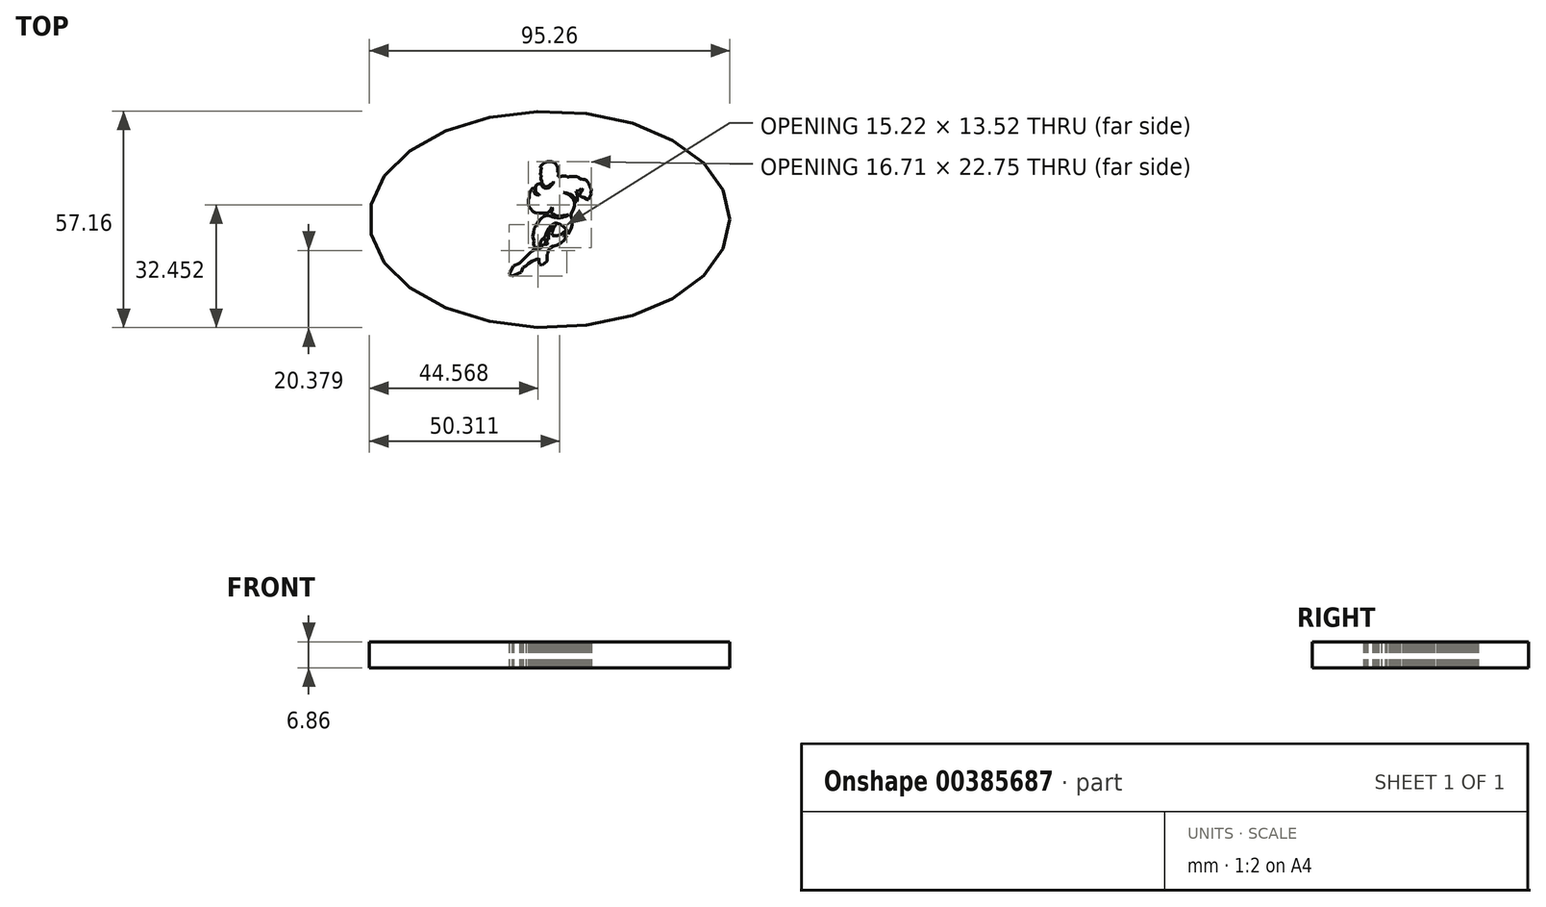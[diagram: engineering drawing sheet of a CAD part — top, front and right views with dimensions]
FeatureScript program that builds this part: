
annotation { "Feature Type Name" : "Feature", "Feature Type Description" : "" }
export const myFeature = defineFeature(function(context is Context, id is Id, definition is map)
    precondition{}
    {
        {
            var Q0;
            Q0=qCreatedBy(makeId("Top.planeOp"),FACE);
            var sketch = newSketch(context, id + "F0", { "sketchPlane" : qUnion([Q0])});
            skEllipse(sketch, "E0", {"center": v(0, 0) * mm, "majorRadius": 47.63 * mm, "minorRadius": 28.58 * mm, "majorAxis": v(1, 0)});
            skLineSegment(sketch, "E1", {"start": v(-10.67, -14.48) * mm, "end": v(-9.93, -14.96) * mm});
            skLineSegment(sketch, "E2", {"start": v(-9.93, -14.96) * mm, "end": v(-7.5, -13.97) * mm});
            skLineSegment(sketch, "E3", {"start": v(-7.5, -13.97) * mm, "end": v(-6.98, -12.63) * mm});
            skLineSegment(sketch, "E4", {"start": v(-6.98, -12.63) * mm, "end": v(-6.3, -12.34) * mm});
            skLineSegment(sketch, "E5", {"start": v(-6.3, -12.34) * mm, "end": v(-5.68, -11.68) * mm});
            skLineSegment(sketch, "E6", {"start": v(-5.68, -11.68) * mm, "end": v(-4.62, -11.01) * mm});
            skLineSegment(sketch, "E7", {"start": v(-4.62, -11.01) * mm, "end": v(-2.83, -10.28) * mm});
            skLineSegment(sketch, "E8", {"start": v(-2.83, -10.28) * mm, "end": v(-2.83, -11.24) * mm});
            skLineSegment(sketch, "E9", {"start": v(-2.83, -11.24) * mm, "end": v(-2.55, -11.87) * mm});
            skLineSegment(sketch, "E10", {"start": v(-2.55, -11.87) * mm, "end": v(-1.92, -12.02) * mm});
            skLineSegment(sketch, "E11", {"start": v(-1.92, -12.02) * mm, "end": v(-0.71, -11.01) * mm});
            skLineSegment(sketch, "E12", {"start": v(-0.71, -11.01) * mm, "end": v(-0.71, -9.22) * mm});
            skLineSegment(sketch, "E13", {"start": v(-0.71, -9.22) * mm, "end": v(-0.37, -8.9) * mm});
            skLineSegment(sketch, "E14", {"start": v(-0.37, -8.9) * mm, "end": v(-0.37, -8.25) * mm});
            skLineSegment(sketch, "E15", {"start": v(-0.37, -8.25) * mm, "end": v(0.2, -7.41) * mm});
            skLineSegment(sketch, "E16", {"start": v(0.2, -7.41) * mm, "end": v(0.84, -7.05) * mm});
            skLineSegment(sketch, "E17", {"start": v(0.84, -7.05) * mm, "end": v(1.82, -6.79) * mm});
            skLineSegment(sketch, "E18", {"start": v(1.82, -6.79) * mm, "end": v(2.96, -6.26) * mm});
            skLineSegment(sketch, "E19", {"start": v(2.96, -6.26) * mm, "end": v(3.94, -5.48) * mm});
            skLineSegment(sketch, "E20", {"start": v(3.94, -5.48) * mm, "end": v(4.55, -4.27) * mm});
            skLineSegment(sketch, "E21", {"start": v(4.55, -4.27) * mm, "end": v(4.1, -4.46) * mm});
            skLineSegment(sketch, "E22", {"start": v(4.1, -4.46) * mm, "end": v(3.73, -4.6) * mm});
            skLineSegment(sketch, "E23", {"start": v(3.73, -4.6) * mm, "end": v(3.61, -4.27) * mm});
            skLineSegment(sketch, "E24", {"start": v(3.61, -4.27) * mm, "end": v(3.85, -3.8) * mm});
            skLineSegment(sketch, "E25", {"start": v(3.85, -3.8) * mm, "end": v(4.29, -3.23) * mm});
            skLineSegment(sketch, "E26", {"start": v(4.29, -3.23) * mm, "end": v(4.29, -2.92) * mm});
            skLineSegment(sketch, "E27", {"start": v(4.29, -2.92) * mm, "end": v(3.55, -3.48) * mm});
            skLineSegment(sketch, "E28", {"start": v(3.55, -3.48) * mm, "end": v(2.96, -3.88) * mm});
            skLineSegment(sketch, "E29", {"start": v(2.96, -3.88) * mm, "end": v(1.96, -4.27) * mm});
            skLineSegment(sketch, "E30", {"start": v(1.96, -4.27) * mm, "end": v(1.6, -4.27) * mm});
            skLineSegment(sketch, "E31", {"start": v(1.6, -4.27) * mm, "end": v(0.96, -4.27) * mm});
            skLineSegment(sketch, "E32", {"start": v(0.96, -4.27) * mm, "end": v(0.72, -4.15) * mm});
            skLineSegment(sketch, "E33", {"start": v(0.72, -4.15) * mm, "end": v(0.57, -3.48) * mm});
            skLineSegment(sketch, "E34", {"start": v(0.57, -3.48) * mm, "end": v(0.8, -2.73) * mm});
            skLineSegment(sketch, "E35", {"start": v(0.8, -2.73) * mm, "end": v(1.16, -2.04) * mm});
            skLineSegment(sketch, "E36", {"start": v(1.16, -2.04) * mm, "end": v(1.52, -1.7) * mm});
            skLineSegment(sketch, "E37", {"start": v(1.52, -1.7) * mm, "end": v(1.52, -1.44) * mm});
            skLineSegment(sketch, "E38", {"start": v(1.52, -1.44) * mm, "end": v(0.57, -2.4) * mm});
            skLineSegment(sketch, "E39", {"start": v(0.57, -2.4) * mm, "end": v(0, -3.06) * mm});
            skLineSegment(sketch, "E40", {"start": v(0, -3.06) * mm, "end": v(-0.25, -3.56) * mm});
            skLineSegment(sketch, "E41", {"start": v(-0.25, -3.56) * mm, "end": v(-0.25, -4.27) * mm});
            skLineSegment(sketch, "E42", {"start": v(-0.25, -4.27) * mm, "end": v(-0.25, -4.93) * mm});
            skLineSegment(sketch, "E43", {"start": v(-0.25, -4.93) * mm, "end": v(-0.25, -5.3) * mm});
            skLineSegment(sketch, "E44", {"start": v(-0.25, -5.3) * mm, "end": v(-0.71, -5.3) * mm});
            skLineSegment(sketch, "E45", {"start": v(-0.71, -5.3) * mm, "end": v(-1.08, -5.48) * mm});
            skLineSegment(sketch, "E46", {"start": v(-1.08, -5.48) * mm, "end": v(-1.38, -5.78) * mm});
            skLineSegment(sketch, "E47", {"start": v(-1.38, -5.78) * mm, "end": v(-1, -5.97) * mm});
            skLineSegment(sketch, "E48", {"start": v(-1, -5.97) * mm, "end": v(-0.71, -6.12) * mm});
            skLineSegment(sketch, "E49", {"start": v(-0.71, -6.12) * mm, "end": v(-0.57, -6.26) * mm});
            skLineSegment(sketch, "E50", {"start": v(-0.57, -6.26) * mm, "end": v(-0.57, -6.42) * mm});
            skLineSegment(sketch, "E51", {"start": v(-0.57, -6.42) * mm, "end": v(-0.67, -6.62) * mm});
            skLineSegment(sketch, "E52", {"start": v(-0.67, -6.62) * mm, "end": v(-1.6, -6.62) * mm});
            skLineSegment(sketch, "E53", {"start": v(-1.6, -6.62) * mm, "end": v(-1.92, -6.79) * mm});
            skLineSegment(sketch, "E54", {"start": v(-1.92, -6.79) * mm, "end": v(-2.1, -7.15) * mm});
            skLineSegment(sketch, "E55", {"start": v(-2.1, -7.15) * mm, "end": v(-2.1, -7.3) * mm});
            skLineSegment(sketch, "E56", {"start": v(-2.1, -7.3) * mm, "end": v(-2.83, -7.76) * mm});
            skLineSegment(sketch, "E57", {"start": v(-2.83, -7.76) * mm, "end": v(-3.27, -7.92) * mm});
            skLineSegment(sketch, "E58", {"start": v(-3.27, -7.92) * mm, "end": v(-3.6, -7.92) * mm});
            skLineSegment(sketch, "E59", {"start": v(-3.6, -7.92) * mm, "end": v(-3.79, -7.82) * mm});
            skLineSegment(sketch, "E60", {"start": v(-3.79, -7.82) * mm, "end": v(-4.48, -8.25) * mm});
            skLineSegment(sketch, "E61", {"start": v(-4.48, -8.25) * mm, "end": v(-5.33, -9.01) * mm});
            skLineSegment(sketch, "E62", {"start": v(-5.33, -9.01) * mm, "end": v(-7.95, -11.55) * mm});
            skLineSegment(sketch, "E63", {"start": v(-7.95, -11.55) * mm, "end": v(-9.63, -12.34) * mm});
            skLineSegment(sketch, "E64", {"start": v(-9.63, -12.34) * mm, "end": v(-10.67, -14.48) * mm});
            skLineSegment(sketch, "E65", {"start": v(2.2, 11.29) * mm, "end": v(2.34, 12.27) * mm});
            skLineSegment(sketch, "E66", {"start": v(2.34, 12.27) * mm, "end": v(2.1, 12.51) * mm});
            skLineSegment(sketch, "E67", {"start": v(2.1, 12.51) * mm, "end": v(2.1, 13.38) * mm});
            skLineSegment(sketch, "E68", {"start": v(2.1, 13.38) * mm, "end": v(2.1, 13.78) * mm});
            skLineSegment(sketch, "E69", {"start": v(2.1, 13.78) * mm, "end": v(1.86, 14.18) * mm});
            skLineSegment(sketch, "E70", {"start": v(1.86, 14.18) * mm, "end": v(1.64, 14.56) * mm});
            skLineSegment(sketch, "E71", {"start": v(1.64, 14.56) * mm, "end": v(1.17, 15.02) * mm});
            skLineSegment(sketch, "E72", {"start": v(1.17, 15.02) * mm, "end": v(0.53, 15.25) * mm});
            skLineSegment(sketch, "E73", {"start": v(0.53, 15.25) * mm, "end": v(-0.53, 15.25) * mm});
            skLineSegment(sketch, "E74", {"start": v(-0.53, 15.25) * mm, "end": v(-1.26, 14.98) * mm});
            skLineSegment(sketch, "E75", {"start": v(-1.26, 14.98) * mm, "end": v(-1.98, 14.52) * mm});
            skLineSegment(sketch, "E76", {"start": v(-1.98, 14.52) * mm, "end": v(-2.16, 14.18) * mm});
            skLineSegment(sketch, "E77", {"start": v(-2.16, 14.18) * mm, "end": v(-2.5, 14.04) * mm});
            skLineSegment(sketch, "E78", {"start": v(-2.5, 14.04) * mm, "end": v(-2.5, 13.78) * mm});
            skLineSegment(sketch, "E79", {"start": v(-2.5, 13.78) * mm, "end": v(-2.34, 13.72) * mm});
            skLineSegment(sketch, "E80", {"start": v(-2.34, 13.72) * mm, "end": v(-2.23, 13.72) * mm});
            skLineSegment(sketch, "E81", {"start": v(-2.23, 13.72) * mm, "end": v(-2.23, 13.34) * mm});
            skLineSegment(sketch, "E82", {"start": v(-2.23, 13.34) * mm, "end": v(-2.35, 13.14) * mm});
            skLineSegment(sketch, "E83", {"start": v(-2.35, 13.14) * mm, "end": v(-2.35, 12.76) * mm});
            skLineSegment(sketch, "E84", {"start": v(-2.35, 12.76) * mm, "end": v(-2.28, 12.66) * mm});
            skLineSegment(sketch, "E85", {"start": v(-2.28, 12.66) * mm, "end": v(-2.28, 12.42) * mm});
            skLineSegment(sketch, "E86", {"start": v(-2.28, 12.42) * mm, "end": v(-2.28, 12.24) * mm});
            skLineSegment(sketch, "E87", {"start": v(-2.28, 12.24) * mm, "end": v(-2.46, 12.17) * mm});
            skLineSegment(sketch, "E88", {"start": v(-2.46, 12.17) * mm, "end": v(-2.46, 11.86) * mm});
            skLineSegment(sketch, "E89", {"start": v(-2.46, 11.86) * mm, "end": v(-2.23, 11.6) * mm});
            skLineSegment(sketch, "E90", {"start": v(-2.23, 11.6) * mm, "end": v(-2.23, 11.3) * mm});
            skLineSegment(sketch, "E91", {"start": v(-2.23, 11.3) * mm, "end": v(-2.32, 11.19) * mm});
            skLineSegment(sketch, "E92", {"start": v(-2.32, 11.19) * mm, "end": v(-2.32, 10.68) * mm});
            skLineSegment(sketch, "E93", {"start": v(-2.32, 10.68) * mm, "end": v(-2.03, 10.04) * mm});
            skLineSegment(sketch, "E94", {"start": v(-2.03, 10.04) * mm, "end": v(-2.03, 9.67) * mm});
            skLineSegment(sketch, "E95", {"start": v(-2.03, 9.67) * mm, "end": v(-1.83, 9.43) * mm});
            skLineSegment(sketch, "E96", {"start": v(-1.83, 9.43) * mm, "end": v(-1.74, 9.17) * mm});
            skLineSegment(sketch, "E97", {"start": v(-1.74, 9.17) * mm, "end": v(-1.74, 8.9) * mm});
            skLineSegment(sketch, "E98", {"start": v(-1.74, 8.9) * mm, "end": v(-1.54, 8.72) * mm});
            skLineSegment(sketch, "E99", {"start": v(-1.54, 8.72) * mm, "end": v(-1.24, 8.63) * mm});
            skLineSegment(sketch, "E100", {"start": v(-1.24, 8.63) * mm, "end": v(-0.77, 8.7) * mm});
            skLineSegment(sketch, "E101", {"start": v(-0.77, 8.7) * mm, "end": v(-0.45, 8.81) * mm});
            skLineSegment(sketch, "E102", {"start": v(-0.45, 8.81) * mm, "end": v(0.1, 9.12) * mm});
            skLineSegment(sketch, "E103", {"start": v(0.1, 9.12) * mm, "end": v(0.57, 9.41) * mm});
            skLineSegment(sketch, "E104", {"start": v(0.57, 9.41) * mm, "end": v(0.91, 9.86) * mm});
            skLineSegment(sketch, "E105", {"start": v(0.91, 9.86) * mm, "end": v(1, 9.99) * mm});
            skLineSegment(sketch, "E106", {"start": v(1, 9.99) * mm, "end": v(1, 9.69) * mm});
            skLineSegment(sketch, "E107", {"start": v(1, 9.69) * mm, "end": v(0.85, 9.46) * mm});
            skLineSegment(sketch, "E108", {"start": v(0.85, 9.46) * mm, "end": v(0.6, 9.1) * mm});
            skLineSegment(sketch, "E109", {"start": v(0.6, 9.1) * mm, "end": v(0.08, 8.65) * mm});
            skLineSegment(sketch, "E110", {"start": v(0.08, 8.65) * mm, "end": v(-0.5, 8.3) * mm});
            skLineSegment(sketch, "E111", {"start": v(-0.5, 8.3) * mm, "end": v(-0.98, 8.3) * mm});
            skLineSegment(sketch, "E112", {"start": v(-0.98, 8.3) * mm, "end": v(-1.4, 8.3) * mm});
            skLineSegment(sketch, "E113", {"start": v(-1.4, 8.3) * mm, "end": v(-1.76, 8.55) * mm});
            skLineSegment(sketch, "E114", {"start": v(-1.76, 8.55) * mm, "end": v(-2.09, 9.08) * mm});
            skLineSegment(sketch, "E115", {"start": v(-2.09, 9.08) * mm, "end": v(-2.09, 9.48) * mm});
            skLineSegment(sketch, "E116", {"start": v(-2.09, 9.48) * mm, "end": v(-2.66, 9.48) * mm});
            skLineSegment(sketch, "E117", {"start": v(-2.66, 9.48) * mm, "end": v(-3.18, 9.3) * mm});
            skLineSegment(sketch, "E118", {"start": v(-3.18, 9.3) * mm, "end": v(-3.57, 9.06) * mm});
            skLineSegment(sketch, "E119", {"start": v(-3.57, 9.06) * mm, "end": v(-3.74, 8.45) * mm});
            skLineSegment(sketch, "E120", {"start": v(-3.74, 8.45) * mm, "end": v(-3.74, 7.87) * mm});
            skLineSegment(sketch, "E121", {"start": v(-3.74, 7.87) * mm, "end": v(-3.58, 7.18) * mm});
            skLineSegment(sketch, "E122", {"start": v(-3.58, 7.18) * mm, "end": v(-3.13, 6.77) * mm});
            skLineSegment(sketch, "E123", {"start": v(-3.13, 6.77) * mm, "end": v(-2.73, 6.53) * mm});
            skLineSegment(sketch, "E124", {"start": v(-2.73, 6.53) * mm, "end": v(-2.73, 6.38) * mm});
            skLineSegment(sketch, "E125", {"start": v(-2.73, 6.38) * mm, "end": v(-3.37, 6.53) * mm});
            skLineSegment(sketch, "E126", {"start": v(-3.37, 6.53) * mm, "end": v(-3.82, 6.8) * mm});
            skLineSegment(sketch, "E127", {"start": v(-3.82, 6.8) * mm, "end": v(-4.17, 7.18) * mm});
            skLineSegment(sketch, "E128", {"start": v(-4.17, 7.18) * mm, "end": v(-4.3, 7.6) * mm});
            skLineSegment(sketch, "E129", {"start": v(-4.3, 7.6) * mm, "end": v(-4.17, 8.28) * mm});
            skLineSegment(sketch, "E130", {"start": v(-4.17, 8.28) * mm, "end": v(-4.56, 8.1) * mm});
            skLineSegment(sketch, "E131", {"start": v(-4.56, 8.1) * mm, "end": v(-5, 7.7) * mm});
            skLineSegment(sketch, "E132", {"start": v(-5, 7.7) * mm, "end": v(-5.27, 7.18) * mm});
            skLineSegment(sketch, "E133", {"start": v(-5.27, 7.18) * mm, "end": v(-5.38, 6.72) * mm});
            skLineSegment(sketch, "E134", {"start": v(-5.38, 6.72) * mm, "end": v(-5.38, 6.33) * mm});
            skLineSegment(sketch, "E135", {"start": v(-5.38, 6.33) * mm, "end": v(-5.38, 5.89) * mm});
            skLineSegment(sketch, "E136", {"start": v(-5.38, 5.89) * mm, "end": v(-5.54, 5.53) * mm});
            skLineSegment(sketch, "E137", {"start": v(-5.54, 5.53) * mm, "end": v(-5.68, 5.21) * mm});
            skLineSegment(sketch, "E138", {"start": v(-5.68, 5.21) * mm, "end": v(-5.68, 4.35) * mm});
            skLineSegment(sketch, "E139", {"start": v(-5.68, 4.35) * mm, "end": v(-5.56, 3.61) * mm});
            skLineSegment(sketch, "E140", {"start": v(-5.56, 3.61) * mm, "end": v(-5.28, 3.05) * mm});
            skLineSegment(sketch, "E141", {"start": v(-5.28, 3.05) * mm, "end": v(-4.92, 2.66) * mm});
            skLineSegment(sketch, "E142", {"start": v(-4.92, 2.66) * mm, "end": v(-4.58, 2.28) * mm});
            skLineSegment(sketch, "E143", {"start": v(-4.58, 2.28) * mm, "end": v(-4.4, 2.08) * mm});
            skLineSegment(sketch, "E144", {"start": v(-4.4, 2.08) * mm, "end": v(-3.89, 1.76) * mm});
            skLineSegment(sketch, "E145", {"start": v(-3.89, 1.76) * mm, "end": v(-3.25, 1.62) * mm});
            skLineSegment(sketch, "E146", {"start": v(-3.25, 1.62) * mm, "end": v(-0.96, 1.62) * mm});
            skLineSegment(sketch, "E147", {"start": v(-0.96, 1.62) * mm, "end": v(-0.43, 1.83) * mm});
            skLineSegment(sketch, "E148", {"start": v(-0.43, 1.83) * mm, "end": v(0, 2.22) * mm});
            skLineSegment(sketch, "E149", {"start": v(0, 2.22) * mm, "end": v(0.3, 2.5) * mm});
            skLineSegment(sketch, "E150", {"start": v(0.3, 2.5) * mm, "end": v(0.48, 3.03) * mm});
            skLineSegment(sketch, "E151", {"start": v(0.48, 3.03) * mm, "end": v(0.6, 3.14) * mm});
            skLineSegment(sketch, "E152", {"start": v(0.6, 3.14) * mm, "end": v(0.7, 2.8) * mm});
            skLineSegment(sketch, "E153", {"start": v(0.7, 2.8) * mm, "end": v(0.7, 2.36) * mm});
            skLineSegment(sketch, "E154", {"start": v(0.7, 2.36) * mm, "end": v(0.43, 1.87) * mm});
            skLineSegment(sketch, "E155", {"start": v(0.43, 1.87) * mm, "end": v(0.43, 1.66) * mm});
            skLineSegment(sketch, "E156", {"start": v(0.43, 1.66) * mm, "end": v(0.8, 1.37) * mm});
            skLineSegment(sketch, "E157", {"start": v(0.8, 1.37) * mm, "end": v(1.44, 1.09) * mm});
            skLineSegment(sketch, "E158", {"start": v(1.44, 1.09) * mm, "end": v(2.09, 0.94) * mm});
            skLineSegment(sketch, "E159", {"start": v(2.09, 0.94) * mm, "end": v(3, 0.94) * mm});
            skLineSegment(sketch, "E160", {"start": v(3, 0.94) * mm, "end": v(3.6, 1) * mm});
            skLineSegment(sketch, "E161", {"start": v(3.6, 1) * mm, "end": v(4.08, 1.05) * mm});
            skLineSegment(sketch, "E162", {"start": v(4.08, 1.05) * mm, "end": v(5, 1.3) * mm});
            skLineSegment(sketch, "E163", {"start": v(5, 1.3) * mm, "end": v(4.8, 1.04) * mm});
            skLineSegment(sketch, "E164", {"start": v(4.8, 1.04) * mm, "end": v(4.33, 0.84) * mm});
            skLineSegment(sketch, "E165", {"start": v(4.33, 0.84) * mm, "end": v(4.04, 0.72) * mm});
            skLineSegment(sketch, "E166", {"start": v(4.04, 0.72) * mm, "end": v(3.38, 0.52) * mm});
            skLineSegment(sketch, "E167", {"start": v(3.38, 0.52) * mm, "end": v(2.8, 0.4) * mm});
            skLineSegment(sketch, "E168", {"start": v(2.8, 0.4) * mm, "end": v(1.97, 0.4) * mm});
            skLineSegment(sketch, "E169", {"start": v(1.97, 0.4) * mm, "end": v(1.24, 0.52) * mm});
            skLineSegment(sketch, "E170", {"start": v(1.24, 0.52) * mm, "end": v(0.72, 0.68) * mm});
            skLineSegment(sketch, "E171", {"start": v(0.72, 0.68) * mm, "end": v(0.1, 0.94) * mm});
            skLineSegment(sketch, "E172", {"start": v(0.1, 0.94) * mm, "end": v(-0.43, 1.09) * mm});
            skLineSegment(sketch, "E173", {"start": v(-0.43, 1.09) * mm, "end": v(-0.68, 1.09) * mm});
            skLineSegment(sketch, "E174", {"start": v(-0.68, 1.09) * mm, "end": v(-1.55, 0.77) * mm});
            skLineSegment(sketch, "E175", {"start": v(-1.55, 0.77) * mm, "end": v(-2.26, 0.22) * mm});
            skLineSegment(sketch, "E176", {"start": v(-2.26, 0.22) * mm, "end": v(-3, -0.57) * mm});
            skLineSegment(sketch, "E177", {"start": v(-3, -0.57) * mm, "end": v(-3.64, -1.67) * mm});
            skLineSegment(sketch, "E178", {"start": v(-3.64, -1.67) * mm, "end": v(-4.05, -2.42) * mm});
            skLineSegment(sketch, "E179", {"start": v(-4.05, -2.42) * mm, "end": v(-4.27, -3.45) * mm});
            skLineSegment(sketch, "E180", {"start": v(-4.27, -3.45) * mm, "end": v(-4.44, -4.6) * mm});
            skLineSegment(sketch, "E181", {"start": v(-4.44, -4.6) * mm, "end": v(-4.05, -5.72) * mm});
            skLineSegment(sketch, "E182", {"start": v(-4.05, -5.72) * mm, "end": v(-4.3, -6.17) * mm});
            skLineSegment(sketch, "E183", {"start": v(-4.3, -6.17) * mm, "end": v(-4.27, -6.63) * mm});
            skLineSegment(sketch, "E184", {"start": v(-4.27, -6.63) * mm, "end": v(-4.08, -7.03) * mm});
            skLineSegment(sketch, "E185", {"start": v(-4.08, -7.03) * mm, "end": v(-3.83, -7.36) * mm});
            skLineSegment(sketch, "E186", {"start": v(-3.83, -7.36) * mm, "end": v(-3.57, -7.5) * mm});
            skLineSegment(sketch, "E187", {"start": v(-3.57, -7.5) * mm, "end": v(-2.84, -7.17) * mm});
            skLineSegment(sketch, "E188", {"start": v(-2.84, -7.17) * mm, "end": v(-2.4, -6.8) * mm});
            skLineSegment(sketch, "E189", {"start": v(-2.4, -6.8) * mm, "end": v(-2.42, -6.35) * mm});
            skLineSegment(sketch, "E190", {"start": v(-2.42, -6.35) * mm, "end": v(-2.31, -5.87) * mm});
            skLineSegment(sketch, "E191", {"start": v(-2.31, -5.87) * mm, "end": v(-2.02, -5.32) * mm});
            skLineSegment(sketch, "E192", {"start": v(-2.02, -5.32) * mm, "end": v(-1.5, -4.78) * mm});
            skLineSegment(sketch, "E193", {"start": v(-1.5, -4.78) * mm, "end": v(-1.16, -4.52) * mm});
            skLineSegment(sketch, "E194", {"start": v(-1.16, -4.52) * mm, "end": v(-0.99, -3.79) * mm});
            skLineSegment(sketch, "E195", {"start": v(-0.99, -3.79) * mm, "end": v(-0.7, -3.18) * mm});
            skLineSegment(sketch, "E196", {"start": v(-0.7, -3.18) * mm, "end": v(-0.19, -2.25) * mm});
            skLineSegment(sketch, "E197", {"start": v(-0.19, -2.25) * mm, "end": v(0.34, -1.62) * mm});
            skLineSegment(sketch, "E198", {"start": v(0.34, -1.62) * mm, "end": v(1.18, -1.03) * mm});
            skLineSegment(sketch, "E199", {"start": v(1.18, -1.03) * mm, "end": v(1.83, -1.03) * mm});
            skLineSegment(sketch, "E200", {"start": v(1.83, -1.03) * mm, "end": v(2.65, -1.28) * mm});
            skLineSegment(sketch, "E201", {"start": v(2.65, -1.28) * mm, "end": v(3.52, -1.75) * mm});
            skLineSegment(sketch, "E202", {"start": v(3.52, -1.75) * mm, "end": v(4.19, -2.42) * mm});
            skLineSegment(sketch, "E203", {"start": v(4.19, -2.42) * mm, "end": v(4.67, -2.94) * mm});
            skLineSegment(sketch, "E204", {"start": v(4.67, -2.94) * mm, "end": v(4.93, -3.91) * mm});
            skLineSegment(sketch, "E205", {"start": v(4.93, -3.91) * mm, "end": v(5.19, -3.43) * mm});
            skPoint(sketch, "E205.endSnap0", {"position": v(4.8, -3.43) * mm});
            skLineSegment(sketch, "E206", {"start": v(5.19, -3.43) * mm, "end": v(5.74, -2.42) * mm});
            skLineSegment(sketch, "E207", {"start": v(5.74, -2.42) * mm, "end": v(5.98, -1.48) * mm});
            skLineSegment(sketch, "E208", {"start": v(5.98, -1.48) * mm, "end": v(5.98, -0.83) * mm});
            skLineSegment(sketch, "E209", {"start": v(5.98, -0.83) * mm, "end": v(5.98, 0) * mm});
            skLineSegment(sketch, "E210", {"start": v(5.98, 0) * mm, "end": v(5.74, 0.83) * mm});
            skLineSegment(sketch, "E211", {"start": v(5.74, 0.83) * mm, "end": v(5.74, 1.6) * mm});
            skLineSegment(sketch, "E212", {"start": v(5.74, 1.6) * mm, "end": v(6.17, 2.4) * mm});
            skLineSegment(sketch, "E213", {"start": v(6.17, 2.4) * mm, "end": v(6.6, 3.51) * mm});
            skLineSegment(sketch, "E214", {"start": v(6.6, 3.51) * mm, "end": v(6.6, 4.11) * mm});
            skLineSegment(sketch, "E215", {"start": v(6.6, 4.11) * mm, "end": v(6.6, 4.6) * mm});
            skLineSegment(sketch, "E216", {"start": v(6.6, 4.6) * mm, "end": v(6.25, 5.2) * mm});
            skLineSegment(sketch, "E217", {"start": v(6.25, 5.2) * mm, "end": v(6.02, 5.63) * mm});
            skLineSegment(sketch, "E218", {"start": v(6.02, 5.63) * mm, "end": v(5.7, 6) * mm});
            skLineSegment(sketch, "E219", {"start": v(5.7, 6) * mm, "end": v(5.39, 6.28) * mm});
            skLineSegment(sketch, "E220", {"start": v(5.39, 6.28) * mm, "end": v(4.65, 6.7) * mm});
            skLineSegment(sketch, "E221", {"start": v(4.65, 6.7) * mm, "end": v(3.67, 7.2) * mm});
            skLineSegment(sketch, "E222", {"start": v(3.67, 7.2) * mm, "end": v(4.34, 7.04) * mm});
            skLineSegment(sketch, "E223", {"start": v(4.34, 7.04) * mm, "end": v(4.82, 6.88) * mm});
            skLineSegment(sketch, "E224", {"start": v(4.82, 6.88) * mm, "end": v(5.39, 6.58) * mm});
            skLineSegment(sketch, "E225", {"start": v(5.39, 6.58) * mm, "end": v(6.04, 6.28) * mm});
            skLineSegment(sketch, "E226", {"start": v(6.04, 6.28) * mm, "end": v(6.51, 5.75) * mm});
            skLineSegment(sketch, "E227", {"start": v(6.51, 5.75) * mm, "end": v(6.84, 5.29) * mm});
            skLineSegment(sketch, "E228", {"start": v(6.84, 5.29) * mm, "end": v(7.04, 4.69) * mm});
            skLineSegment(sketch, "E229", {"start": v(7.04, 4.69) * mm, "end": v(7.14, 4.72) * mm});
            skLineSegment(sketch, "E230", {"start": v(7.14, 4.72) * mm, "end": v(7.28, 5.2) * mm});
            skLineSegment(sketch, "E231", {"start": v(7.28, 5.2) * mm, "end": v(7.28, 5.73) * mm});
            skLineSegment(sketch, "E232", {"start": v(7.28, 5.73) * mm, "end": v(7.3, 6.2) * mm});
            skLineSegment(sketch, "E233", {"start": v(7.3, 6.2) * mm, "end": v(7.15, 6.9) * mm});
            skLineSegment(sketch, "E234", {"start": v(7.15, 6.9) * mm, "end": v(6.9, 7.57) * mm});
            skLineSegment(sketch, "E235", {"start": v(6.9, 7.57) * mm, "end": v(7.6, 7.57) * mm});
            skLineSegment(sketch, "E236", {"start": v(7.6, 7.57) * mm, "end": v(8.02, 7.74) * mm});
            skLineSegment(sketch, "E237", {"start": v(8.02, 7.74) * mm, "end": v(8.38, 8.19) * mm});
            skLineSegment(sketch, "E238", {"start": v(8.38, 8.19) * mm, "end": v(8.68, 7.94) * mm});
            skLineSegment(sketch, "E239", {"start": v(8.68, 7.94) * mm, "end": v(8.9, 7.79) * mm});
            skLineSegment(sketch, "E240", {"start": v(8.9, 7.79) * mm, "end": v(8.83, 7.7) * mm});
            skLineSegment(sketch, "E241", {"start": v(8.83, 7.7) * mm, "end": v(8.62, 7.7) * mm});
            skLineSegment(sketch, "E242", {"start": v(8.62, 7.7) * mm, "end": v(8.6, 7.57) * mm});
            skLineSegment(sketch, "E243", {"start": v(8.6, 7.57) * mm, "end": v(8.46, 7.57) * mm});
            skLineSegment(sketch, "E244", {"start": v(8.46, 7.57) * mm, "end": v(8.45, 7.36) * mm});
            skLineSegment(sketch, "E245", {"start": v(8.45, 7.36) * mm, "end": v(8.33, 7.32) * mm});
            skLineSegment(sketch, "E246", {"start": v(8.33, 7.32) * mm, "end": v(8.36, 7.23) * mm});
            skLineSegment(sketch, "E247", {"start": v(8.36, 7.23) * mm, "end": v(8.2, 7.09) * mm});
            skLineSegment(sketch, "E248", {"start": v(8.2, 7.09) * mm, "end": v(8.12, 6.93) * mm});
            skLineSegment(sketch, "E249", {"start": v(8.12, 6.93) * mm, "end": v(8.01, 6.82) * mm});
            skLineSegment(sketch, "E250", {"start": v(8.01, 6.82) * mm, "end": v(7.93, 6.42) * mm});
            skLineSegment(sketch, "E251", {"start": v(7.93, 6.42) * mm, "end": v(8.46, 5.85) * mm});
            skLineSegment(sketch, "E252", {"start": v(8.46, 5.85) * mm, "end": v(8.95, 5.85) * mm});
            skLineSegment(sketch, "E253", {"start": v(8.95, 5.85) * mm, "end": v(9.98, 5.27) * mm});
            skLineSegment(sketch, "E254", {"start": v(9.98, 5.27) * mm, "end": v(10.24, 5.25) * mm});
            skLineSegment(sketch, "E255", {"start": v(10.24, 5.25) * mm, "end": v(11.04, 6.74) * mm});
            skLineSegment(sketch, "E256", {"start": v(11.04, 6.74) * mm, "end": v(10.94, 7.05) * mm});
            skLineSegment(sketch, "E257", {"start": v(10.94, 7.05) * mm, "end": v(10.97, 7.85) * mm});
            skLineSegment(sketch, "E258", {"start": v(10.97, 7.85) * mm, "end": v(10.77, 8.42) * mm});
            skLineSegment(sketch, "E259", {"start": v(10.77, 8.42) * mm, "end": v(10.32, 9.36) * mm});
            skLineSegment(sketch, "E260", {"start": v(10.32, 9.36) * mm, "end": v(9.74, 10.25) * mm});
            skLineSegment(sketch, "E261", {"start": v(9.74, 10.25) * mm, "end": v(9.28, 10.61) * mm});
            skLineSegment(sketch, "E262", {"start": v(9.28, 10.61) * mm, "end": v(8.9, 10.61) * mm});
            skLineSegment(sketch, "E263", {"start": v(8.9, 10.61) * mm, "end": v(8.35, 10.68) * mm});
            skLineSegment(sketch, "E264", {"start": v(8.35, 10.68) * mm, "end": v(8, 10.68) * mm});
            skLineSegment(sketch, "E265", {"start": v(8, 10.68) * mm, "end": v(7.65, 11.02) * mm});
            skLineSegment(sketch, "E266", {"start": v(7.65, 11.02) * mm, "end": v(7.05, 11.3) * mm});
            skLineSegment(sketch, "E267", {"start": v(7.05, 11.3) * mm, "end": v(6.57, 11.33) * mm});
            skLineSegment(sketch, "E268", {"start": v(6.57, 11.33) * mm, "end": v(5.82, 11.36) * mm});
            skLineSegment(sketch, "E269", {"start": v(5.82, 11.36) * mm, "end": v(5.15, 11.36) * mm});
            skLineSegment(sketch, "E270", {"start": v(5.15, 11.36) * mm, "end": v(4.98, 11.21) * mm});
            skLineSegment(sketch, "E271", {"start": v(4.98, 11.21) * mm, "end": v(4.71, 11.24) * mm});
            skLineSegment(sketch, "E272", {"start": v(4.71, 11.24) * mm, "end": v(4.4, 11.48) * mm});
            skLineSegment(sketch, "E273", {"start": v(4.4, 11.48) * mm, "end": v(3.85, 11.5) * mm});
            skLineSegment(sketch, "E274", {"start": v(3.85, 11.5) * mm, "end": v(3.25, 11.45) * mm});
            skLineSegment(sketch, "E275", {"start": v(3.25, 11.45) * mm, "end": v(2.98, 11.33) * mm});
            skLineSegment(sketch, "E276", {"start": v(2.98, 11.33) * mm, "end": v(2.74, 11.3) * mm});
            skLineSegment(sketch, "E277", {"start": v(2.74, 11.3) * mm, "end": v(2.4, 11.3) * mm});
            skLineSegment(sketch, "E278", {"start": v(2.4, 11.3) * mm, "end": v(2.2, 11.29) * mm});
            skLineSegment(sketch, "E279", {"start": v(-3.43, 3.01) * mm, "end": v(-2.27, 3.01) * mm});
            skLineSegment(sketch, "E280", {"start": v(-2.27, 3.01) * mm, "end": v(-1.81, 3.22) * mm});
            skLineSegment(sketch, "E281", {"start": v(-1.81, 3.22) * mm, "end": v(-1.3, 3.58) * mm});
            skLineSegment(sketch, "E282", {"start": v(-1.3, 3.58) * mm, "end": v(-1.17, 4.14) * mm});
            skLineSegment(sketch, "E283", {"start": v(-1.17, 4.14) * mm, "end": v(-1.34, 4.54) * mm});
            skLineSegment(sketch, "E284", {"start": v(-1.34, 4.54) * mm, "end": v(-1.52, 4.9) * mm});
            skLineSegment(sketch, "E285", {"start": v(-1.52, 4.9) * mm, "end": v(-1.72, 5.23) * mm});
            skLineSegment(sketch, "E286", {"start": v(-1.72, 5.23) * mm, "end": v(-2.12, 5.61) * mm});
            skLineSegment(sketch, "E287", {"start": v(-2.12, 5.61) * mm, "end": v(-1.96, 5.64) * mm});
            skLineSegment(sketch, "E288", {"start": v(-1.96, 5.64) * mm, "end": v(-1.54, 5.5) * mm});
            skLineSegment(sketch, "E289", {"start": v(-1.54, 5.5) * mm, "end": v(-1.01, 4.93) * mm});
            skLineSegment(sketch, "E290", {"start": v(-1.01, 4.93) * mm, "end": v(-0.76, 4.58) * mm});
            skLineSegment(sketch, "E291", {"start": v(-0.76, 4.58) * mm, "end": v(-0.51, 4.06) * mm});
            skLineSegment(sketch, "E292", {"start": v(-0.51, 4.06) * mm, "end": v(-0.4, 3.68) * mm});
            skLineSegment(sketch, "E293", {"start": v(-0.4, 3.68) * mm, "end": v(-0.04, 3.56) * mm});
            skLineSegment(sketch, "E294", {"start": v(-0.04, 3.56) * mm, "end": v(0.2, 3.76) * mm});
            skLineSegment(sketch, "E295", {"start": v(0.2, 3.76) * mm, "end": v(0.33, 4.04) * mm});
            skLineSegment(sketch, "E296", {"start": v(0.33, 4.04) * mm, "end": v(0.42, 4.44) * mm});
            skLineSegment(sketch, "E297", {"start": v(0.42, 4.44) * mm, "end": v(0.28, 4.73) * mm});
            skLineSegment(sketch, "E298", {"start": v(0.28, 4.73) * mm, "end": v(0.12, 5.04) * mm});
            skLineSegment(sketch, "E299", {"start": v(0.12, 5.04) * mm, "end": v(-0.22, 5.38) * mm});
            skLineSegment(sketch, "E300", {"start": v(-0.22, 5.38) * mm, "end": v(-0.62, 5.63) * mm});
            skLineSegment(sketch, "E301", {"start": v(-0.62, 5.63) * mm, "end": v(-1.09, 5.86) * mm});
            skLineSegment(sketch, "E302", {"start": v(-1.09, 5.86) * mm, "end": v(-1.56, 5.97) * mm});
            skLineSegment(sketch, "E303", {"start": v(-1.56, 5.97) * mm, "end": v(-1.93, 5.98) * mm});
            skLineSegment(sketch, "E304", {"start": v(-1.93, 5.98) * mm, "end": v(-2.31, 5.96) * mm});
            skLineSegment(sketch, "E305", {"start": v(-2.31, 5.96) * mm, "end": v(-2.76, 5.79) * mm});
            skLineSegment(sketch, "E306", {"start": v(-2.76, 5.79) * mm, "end": v(-2.96, 5.58) * mm});
            skLineSegment(sketch, "E307", {"start": v(-2.96, 5.58) * mm, "end": v(-3.22, 5.35) * mm});
            skLineSegment(sketch, "E308", {"start": v(-3.22, 5.35) * mm, "end": v(-3.4, 5.14) * mm});
            skLineSegment(sketch, "E309", {"start": v(-3.4, 5.14) * mm, "end": v(-3.6, 4.93) * mm});
            skLineSegment(sketch, "E310", {"start": v(-3.6, 4.93) * mm, "end": v(-3.72, 4.7) * mm});
            skLineSegment(sketch, "E311", {"start": v(-3.72, 4.7) * mm, "end": v(-3.87, 4.27) * mm});
            skLineSegment(sketch, "E312", {"start": v(-3.87, 4.27) * mm, "end": v(-3.88, 4) * mm});
            skLineSegment(sketch, "E313", {"start": v(-3.88, 4) * mm, "end": v(-3.87, 3.77) * mm});
            skLineSegment(sketch, "E314", {"start": v(-3.87, 3.77) * mm, "end": v(-3.75, 3.93) * mm});
            skLineSegment(sketch, "E315", {"start": v(-3.75, 3.93) * mm, "end": v(-3.63, 4.14) * mm});
            skLineSegment(sketch, "E316", {"start": v(-3.63, 4.14) * mm, "end": v(-3.48, 4.13) * mm});
            skLineSegment(sketch, "E317", {"start": v(-3.48, 4.13) * mm, "end": v(-3.38, 3.75) * mm});
            skLineSegment(sketch, "E318", {"start": v(-3.38, 3.75) * mm, "end": v(-3.38, 3.37) * mm});
            skLineSegment(sketch, "E319", {"start": v(-3.38, 3.37) * mm, "end": v(-3.43, 3.01) * mm});
            skSolve(sketch);
        }
        {
            var Q0;
            Q0=makeQuery(id+"F0.imprint","IMPRINT",FACE,{"disambiguationData":[TD([[makeQuery(id+"F0.imprint","IMPRINT",EDGE,{"derivedFrom":sQuery(id+"F0.wireOp",EDGE,"E0")}),1.0]])]});
            extrude(context, id + "F1", {"entities" : qUnion([Q0]), "depth" : 6.86 * mm});
        }
    });
